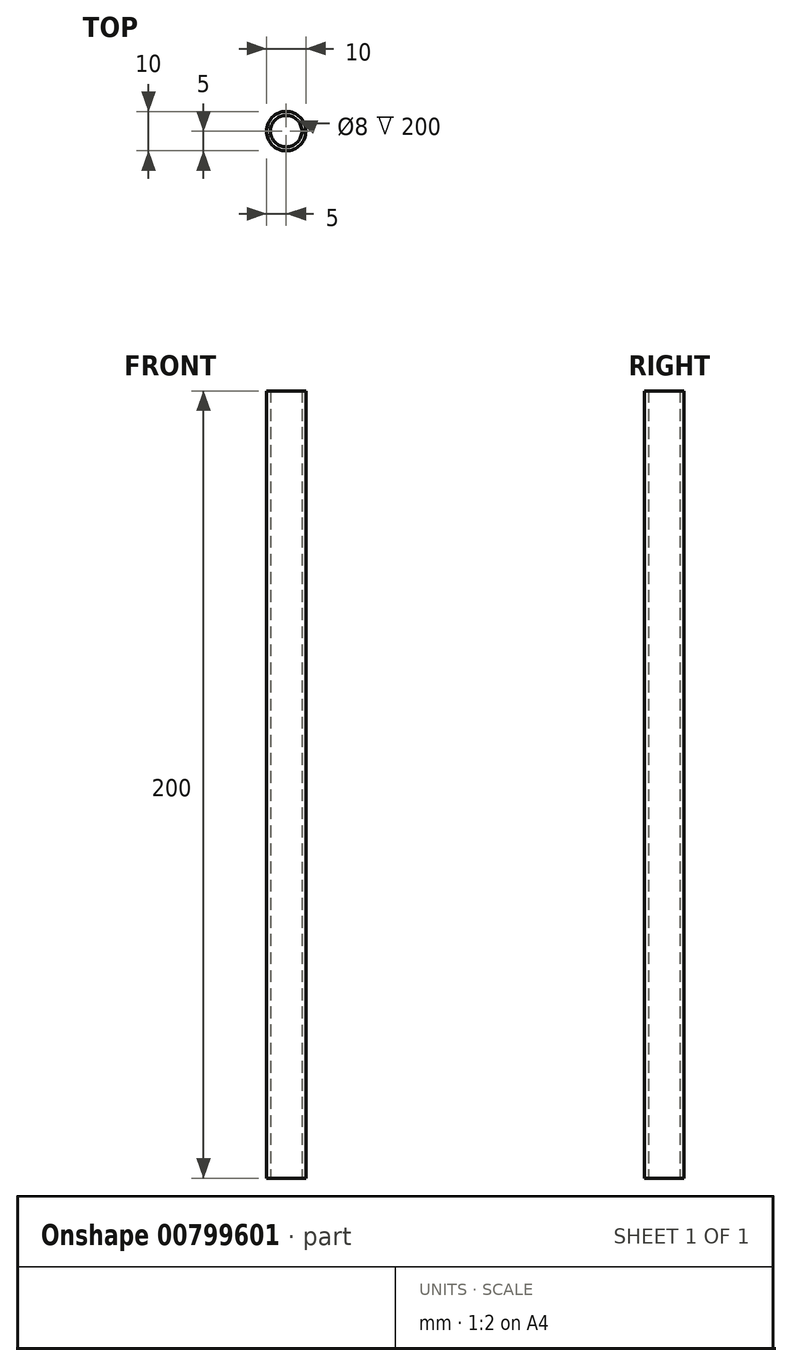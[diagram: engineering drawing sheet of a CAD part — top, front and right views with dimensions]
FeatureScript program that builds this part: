
annotation { "Feature Type Name" : "Feature", "Feature Type Description" : "" }
export const myFeature = defineFeature(function(context is Context, id is Id, definition is map)
    precondition{}
    {
        {
            var Q0;
            Q0=qCreatedBy(makeId("Top.planeOp"),FACE);
            var sketch = newSketch(context, id + "F0", { "sketchPlane" : qUnion([Q0])});
            skCircle(sketch, "E0", {"center": v(0, 0) * mm, "radius": 5 * mm});
            skCircle(sketch, "E1", {"center": v(0, 0) * mm, "radius": 4 * mm});
            skSolve(sketch);
        }
        {
            var Q0;
            Q0=makeQuery(id+"F0.imprint","IMPRINT",FACE,{"disambiguationData":[TD([[makeQuery(id+"F0.imprint","IMPRINT",EDGE,{"derivedFrom":sQuery(id+"F0.wireOp",EDGE,"E0")}),1.0]])]});
            extrude(context, id + "F1", {"entities" : qUnion([Q0]), "depth" : 200 * mm, "offsetDistance" : 25 * mm});
        }
    });
